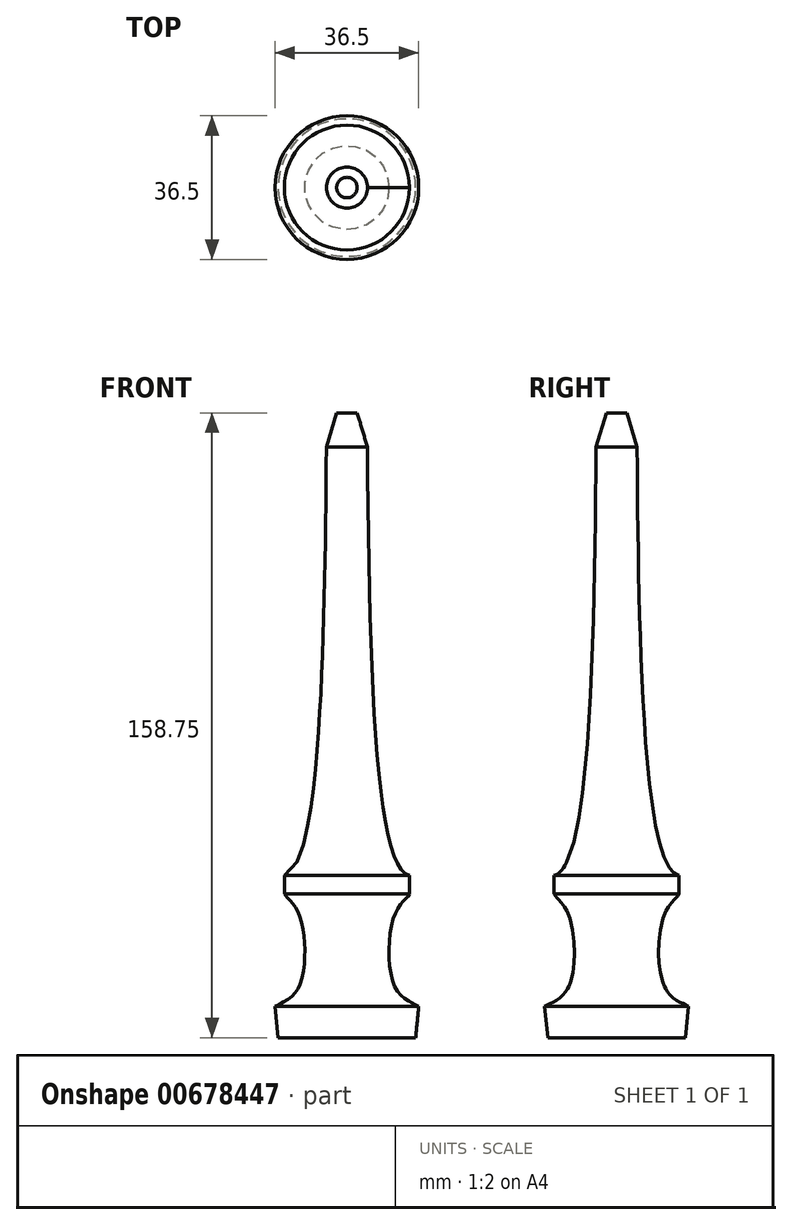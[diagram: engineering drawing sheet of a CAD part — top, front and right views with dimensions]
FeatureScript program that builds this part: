
annotation { "Feature Type Name" : "Feature", "Feature Type Description" : "" }
export const myFeature = defineFeature(function(context is Context, id is Id, definition is map)
    precondition{}
    {
        {
            var Q0;
            Q0=qCreatedBy(makeId("Front.planeOp"),FACE);
            var sketch = newSketch(context, id + "F0", { "sketchPlane" : qUnion([Q0])});
            skLineSegment(sketch, "E0", {"start": v(0, 80.95) * mm, "end": v(0, -69.19) * mm, "construction": true});
            skLineSegment(sketch, "E1", {"start": v(0, -69.19) * mm, "end": v(-17.46, -69.19) * mm});
            skLineSegment(sketch, "E2", {"start": v(0, -61.26) * mm, "end": v(-18.25, -61.26) * mm});
            skLineSegment(sketch, "E3", {"start": v(0, -32.69) * mm, "end": v(-15.87, -32.69) * mm});
            skLineSegment(sketch, "E4", {"start": v(0, -27.94) * mm, "end": v(-15.87, -27.94) * mm});
            skLineSegment(sketch, "E5", {"start": v(0, 89.56) * mm, "end": v(-2.6, 89.56) * mm});
            skLineSegment(sketch, "E6", {"start": v(-2.6, 89.56) * mm, "end": v(-5.2, 80.95) * mm});
            skFitSpline(sketch, "E7", {"points": [v(-5.2, 80.95) * mm, v(-15.87, -27.94) * mm, v(-46.45, 37.7) * mm], "startDerivative": vector(-2.36, -318.22) * mm, "endDerivative": vector(-79.18, 249.82) * mm});
            skLineSegment(sketch, "E8", {"start": v(-15.88, -27.94) * mm, "end": v(-15.87, -32.69) * mm});
            skLineSegment(sketch, "E9", {"start": v(0, 89.56) * mm, "end": v(0, -69.19) * mm});
            skFitSpline(sketch, "E10", {"points": [v(-15.87, -32.69) * mm, v(-12.45, -37.22) * mm, v(-12.45, -56.74) * mm, v(-18.25, -61.26) * mm], "startDerivative": vector(6.9, -13.4) * mm, "endDerivative": vector(-17.13, -10.62) * mm});
            skLineSegment(sketch, "E11", {"start": v(-17.46, -69.19) * mm, "end": v(-18.25, -61.26) * mm});
            skSolve(sketch);
        }
        {
            var Q0;
            {var subQ0=sQuery(id+"F0.wireOp",EDGE,"E3");Q0=makeQuery(id+"F0.imprint","IMPRINT",FACE,{"disambiguationData":[TD([[makeQuery(id+"F0.imprint","IMPRINT",EDGE,{"derivedFrom":subQ0}),-1.0]])]});}
            var Q1;
            {var subQ0=sQuery(id+"F0.wireOp",EDGE,"E2");Q1=makeQuery(id+"F0.imprint","IMPRINT",FACE,{"disambiguationData":[TD([[makeQuery(id+"F0.imprint","IMPRINT",EDGE,{"derivedFrom":subQ0}),-1.0]])]});}
            var Q2;
            {var subQ1=sQuery(id+"F0.wireOp",EDGE,"E4");Q2=makeQuery(id+"F0.imprint","IMPRINT",FACE,{"disambiguationData":[TD([[makeQuery(id+"F0.imprint","IMPRINT",EDGE,{"derivedFrom":subQ1}),-1.0]])]});}
            var Q3;
            {var subQ0=sQuery(id+"F0.wireOp",EDGE,"E1");Q3=makeQuery(id+"F0.imprint","IMPRINT",FACE,{"disambiguationData":[TD([[makeQuery(id+"F0.imprint","IMPRINT",EDGE,{"derivedFrom":subQ0}),-1.0]])]});}
            var Q4;
            Q4=sQuery(id+"F0.wireOp",EDGE,"E9");
            revolve(context, id + "F1", {"entities" : qUnion([Q0, Q1, Q2, Q3]), "axis" : qUnion([Q4]), "revolveType" : RevolveType.FULL});
        }
    });
